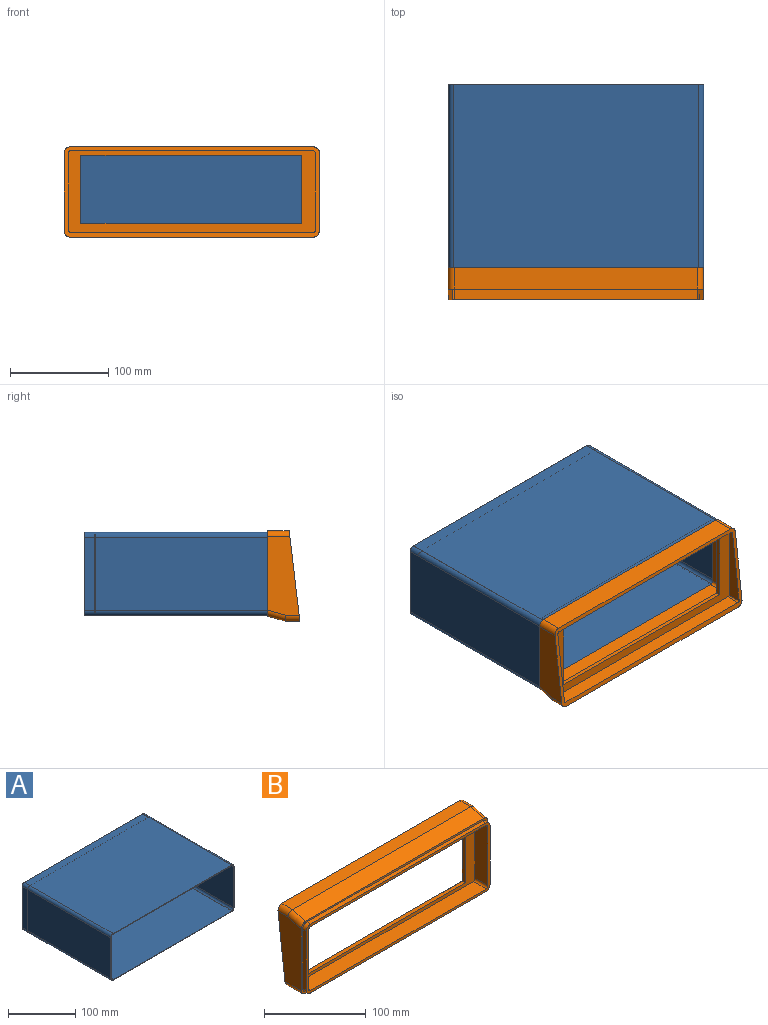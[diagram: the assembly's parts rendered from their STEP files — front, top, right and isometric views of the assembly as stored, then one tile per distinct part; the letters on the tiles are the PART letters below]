
ASSEMBLY  parts=2 mates=2
PART A: 28 faces, bbox 260x187x85 mm
  f0: plane 260x85mm, normal (0,1,0), area 677.4mm2, adj f1,f2,f3,f4,f5,f6,f7,f8
  f1: plane 250x187mm, normal (0,0,1), area 46750mm2, adj f0,f2,f8,f9
  f2: cylinder r=5mm len=187mm, axis (0,-1,0), area 1468.7mm2, adj f0,f1,f3,f9
  f3: plane 187x75mm, normal (-1,0,0), area 14025mm2, adj f0,f2,f4,f9
  f4: cylinder r=5mm len=187mm, axis (0,-1,0), area 1468.7mm2, adj f0,f3,f5,f9
  f5: plane 250x187mm, normal (0,0,-1), area 46750mm2, adj f0,f4,f6,f9
  f6: cylinder r=5mm len=187mm, axis (0,-1,0), area 1468.7mm2, adj f0,f5,f7,f9
  f7: plane 187x75mm, normal (1,0,0), area 14025mm2, adj f0,f6,f8,f9
  f8: cylinder r=5mm len=187mm, axis (0,-1,0), area 1468.7mm2, adj f0,f1,f7,f9
  f9: plane 260x85mm, normal (0,-1,0), area 677.4mm2, adj f1,f2,f3,f4,f5,f6,f7,f8
  f10: plane 251x175mm, normal (0,0,-1), area 43925mm2, adj f9,f11,f17,f18
  f11: cylinder r=4mm len=175mm, axis (0,-1,0), area 1099.6mm2, adj f9,f10,f12,f18
  f12: plane 175x75mm, normal (1,0,0), area 13125mm2, adj f9,f11,f13,f18
  f13: cylinder r=4mm len=175mm, axis (0,-1,0), area 1099.6mm2, adj f9,f12,f14,f18
  f14: plane 251x175mm, normal (0,0,1), area 43925mm2, adj f9,f13,f15,f18
  f15: cylinder r=4mm len=175mm, axis (0,-1,0), area 922.7mm2, adj f9,f14,f16,f18
  f16: plane 175x75.25mm, normal (-1,0,0), area 13169.5mm2, adj f9,f15,f17,f18
  f17: cylinder r=4mm len=175mm, axis (0,-1,0), area 922.7mm2, adj f9,f10,f16,f18
  f18: plane 258x83mm, normal (0,-1,0), area 21401.1mm2, adj f10,f11,f12,f13,f14,f15,f16,f17
  f19: plane 75.25x11mm, normal (-1,0,0), area 827.8mm2, adj f0,f20,f26,f27
  f20: cylinder r=4mm len=11mm, axis (0,1,0), area 58mm2, adj f0,f19,f21,f27
  f21: plane 251x11mm, normal (0,0,1), area 2761mm2, adj f0,f20,f22,f27
  f22: cylinder r=4mm len=11mm, axis (0,1,0), area 69.1mm2, adj f0,f21,f23,f27
  f23: plane 75x11mm, normal (1,0,0), area 825mm2, adj f0,f22,f24,f27
  f24: cylinder r=4mm len=11mm, axis (0,1,0), area 69.1mm2, adj f0,f23,f25,f27
  f25: plane 251x11mm, normal (0,0,-1), area 2761mm2, adj f0,f24,f26,f27
  f26: cylinder r=4mm len=11mm, axis (0,1,0), area 58mm2, adj f0,f19,f25,f27
  f27: plane 258x83mm, normal (0,1,0), area 21401.1mm2, adj f19,f20,f21,f22,f23,f24,f25,f26
PART B: 44 faces, bbox 260x38x92 mm
  f0: plane 250x77mm, normal (0,-1,0), area 3567.4mm2, adj f24,f25,f26,f27,f28,f29,f30,f31
  f1: plane 252x83mm, normal (0,1,0), area 5237.7mm2, adj f32,f33,f34,f35,f36,f37,f38,f39
  f2: plane 256x83mm, normal (0,-1,0), area 1974.5mm2, adj f4,f5,f12,f13,f14,f17,f19,f22
  f3: plane 80x32.28mm, normal (1,0,0), area 2150.8mm2, adj f7,f10,f15,f16,f18
  f4: plane 244x5mm, normal (0,0,1), area 1220mm2, adj f2,f10,f14,f19
  f5: plane 244x5mm, normal (0,0,-1), area 1220mm2, adj f2,f10,f17,f22
  f6: plane 80x32.28mm, normal (-1,0,0), area 2150.8mm2, adj f7,f10,f20,f21,f23
  f7: plane 260x92mm, normal (0,0.99,-0.12), area 2997.5mm2, adj f3,f6,f8,f11,f15,f18,f20,f23
  f8: plane 248x15mm, normal (0,0,1), area 3720mm2, adj f7,f9,f15,f20
  f9: plane 248x18mm, normal (0,-0.27,0.96), area 4633mm2, adj f8,f10,f16,f21
  f10: plane 260x87mm, normal (0,-1,0), area 1371.4mm2, adj f3,f4,f5,f6,f9,f11,f12,f13
  f11: plane 248x22mm, normal (0,0,-1), area 5456mm2, adj f7,f10,f18,f23
  f12: plane 71x5mm, normal (-1,0,0), area 355mm2, adj f2,f10,f19,f22
  f13: plane 71x5mm, normal (1,0,0), area 355mm2, adj f2,f10,f14,f17
  f14: cylinder r=6mm len=6mm, axis (0,-1,0), area 47.1mm2, adj f2,f4,f10,f13
  f15: cylinder r=6mm len=15mm, axis (0,-1,0), area 136.1mm2, adj f3,f7,f8,f16
  f16: cylinder r=6mm len=21.21mm, axis (0,-0.96,-0.27), area 179mm2, adj f3,f9,f10,f15
  f17: cylinder r=6mm len=6mm, axis (0,1,0), area 47.1mm2, adj f2,f5,f10,f13
  f18: cylinder r=6mm len=22.72mm, axis (0,1,0), area 209.8mm2, adj f3,f7,f10,f11
  f19: cylinder r=6mm len=6mm, axis (0,-1,0), area 47.1mm2, adj f2,f4,f10,f12
  f20: cylinder r=6mm len=15mm, axis (0,1,0), area 136.1mm2, adj f6,f7,f8,f21
  f21: cylinder r=6mm len=21.21mm, axis (0,0.96,0.27), area 179mm2, adj f6,f9,f10,f20
  f22: cylinder r=6mm len=6mm, axis (0,1,0), area 47.1mm2, adj f2,f5,f10,f12
  f23: cylinder r=6mm len=22.72mm, axis (0,-1,0), area 209.8mm2, adj f6,f7,f10,f11
  f24: plane 244x18mm, normal (0,0,-1), area 4392mm2, adj f0,f2,f25,f31
  f25: cylinder r=3mm len=18mm, axis (0,-1,0), area 84.8mm2, adj f0,f2,f24,f26
  f26: plane 71x18mm, normal (1,0,0), area 1278mm2, adj f0,f2,f25,f27
  f27: cylinder r=3mm len=18mm, axis (0,-1,0), area 84.8mm2, adj f0,f2,f26,f28
  f28: plane 244.87x18mm, normal (0,0,1), area 4407.6mm2, adj f0,f2,f27,f29
  f29: cylinder r=3mm len=18mm, axis (0,-1,0), area 69mm2, adj f0,f2,f28,f30
  f30: plane 71.13x18mm, normal (-1,0,0), area 1280.3mm2, adj f0,f2,f29,f31
  f31: cylinder r=3mm len=18mm, axis (0,-1,0), area 84.8mm2, adj f0,f2,f24,f30
  f32: plane 247.99x4.48mm, normal (0,0,1), area 1110.6mm2, adj f1,f7,f33,f39
  f33: cylinder r=2mm len=4.72mm, axis (0,1,0), area 14.4mm2, adj f1,f7,f32,f34
  f34: plane 80x14.28mm, normal (-1,0,0), area 760mm2, adj f1,f7,f33,f35
  f35: cylinder r=2.51mm len=14.4mm, axis (0,1,0), area 33.3mm2, adj f1,f7,f34,f36
  f36: plane 248x14.4mm, normal (0,0,-1), area 3571.7mm2, adj f1,f7,f35,f37
  f37: cylinder r=2mm len=14.4mm, axis (0,1,0), area 43.7mm2, adj f1,f7,f36,f38
  f38: plane 79.09x14.17mm, normal (1,0,0), area 747mm2, adj f1,f7,f37,f39
  f39: cylinder r=2mm len=4.72mm, axis (0,1,0), area 14.4mm2, adj f1,f7,f32,f38
  f40: plane 225.1x5mm, normal (0,-0.12,-0.99), area 1133.5mm2, adj f0,f1,f41,f43
  f41: plane 70.24x5mm, normal (-1,0,0), area 348.2mm2, adj f0,f1,f40,f42
  f42: plane 225.1x5mm, normal (0,0.12,0.99), area 1133.5mm2, adj f0,f1,f41,f43
  f43: plane 70.24x5mm, normal (1,0,0), area 348.2mm2, adj f0,f1,f40,f42
PLACE A t=(-3.9,3.46,0.78)mm
PLACE B rot(axis=(1,0,0),180deg) t=(255.51,8.31,80.07)mm
MATE parallel B.f13 <-> A.f16  axis (1,0,0) through (253.51,5.81,36.57)mm
MATE parallel B.f4 <-> A.f1  axis (0,0,-1) through (125.51,5.81,-4.93)mm
